# Revit family: Storage-Teknion-PLT_S_Locker_Tower_Standard-R2015
name_source: partatom
category: Furniture
revit_build: Autodesk Revit Architecture 2015 (Build: 20140323_1530(x64)
units: mm (PartAtom-declared; Revit-internal decimal feet)

## types (6) — shared parameters
Assembly Code = E2020200
District Handle Length 1 = -5.28 "
District Handle Length 2 = -3.03 "
Manufacturer = Teknion
Manufacturer Fax = 416.661.4586
Product Documentation Link = http://www.teknion.com
Product Line = Filing and Storage
Product Page URL = http://www.teknion.com
Series = Ledger Plus
Sustainability Data = http://www.teknion.com
URL = www.teknion.com
Unit Weight URL = http://www.teknion.com
Warranty = http://www.teknion.com

## per-type parameters (varying)
| type | Description | Dual Locker | Dual Locker Vertical Depth | Lock Visibility 1 | Lock Visibility 10 | Lock Visibility 11 | Lock Visibility 12 | Lock Visibility 2 | Lock Visibility 3 | Lock Visibility 4 | Lock Visibility 5 | Lock Visibility 6 | Lock Visibility 7 | Lock Visibility 8 | Lock Visibility 9 | Model | One High | Part Number | Three High | Triple Locker | Triple Locker Vertical Depth | Two High | three high Horizontal Depth | two high Horizontal Depth |
| Dual Locker Tower - Standard - One High | Dual Locker Tower - Standard, Freestanding, One-High | Yes | 6 " | No | Yes | No | Yes | No | No | No | No | No | No | No | No | PLTDS_1_ | Yes | PLTDS | No | No | 1 " | No | 1 " | 1 " |
| Dual Locker Tower - Standard - Two High | Dual Locker Tower - Standard, Freestanding, Two-High | Yes | 6 " | Yes | No | No | No | No | Yes | No | Yes | Yes | No | No | No | PLTDS_2_ | No | PLTDS | No | No | 1 " | Yes | 1 " | 6 " |
| Dual Locker Tower - Standard - Three High | Dual Locker Tower - Standard, Freestanding, Three-High | Yes | 6 " | Yes | No | No | No | No | Yes | Yes | No | No | No | Yes | No | PLTDS_3_ | No | PLTDS | Yes | No | 1 " | No | 6 " | 1 " |
| Triple Locker Tower - Standard - One High | Triple Locker Tower - Standard, Freestanding, One-High | No | 1 " | No | No | Yes | Yes | No | No | No | No | No | No | No | No | PLTTS_1_ | Yes | PLTTS | No | Yes | 6 " | No | 1 " | 1 " |
| Triple Locker Tower - Standard - Two High | Triple Locker Tower - Standard, Freestanding, Two-High | No | 1 " | Yes | No | No | No | Yes | No | No | Yes | No | Yes | No | No | PLTTS_2_ | No | PLTTS | No | Yes | 6 " | Yes | 1 " | 6 " |
| Triple Locker Tower - Standard - Three High | Triple Locker Tower - Standard, Freestanding, Three-High | No | 1 " | Yes | No | No | No | Yes | No | Yes | No | No | No | No | Yes | PLTTS_3_ | No | PLTTS | Yes | Yes | 6 " | No | 6 " | 1 " |

## geometry (parser evidence)
native form markers: Sweep x3
no freeform markers — native parametric forms only
